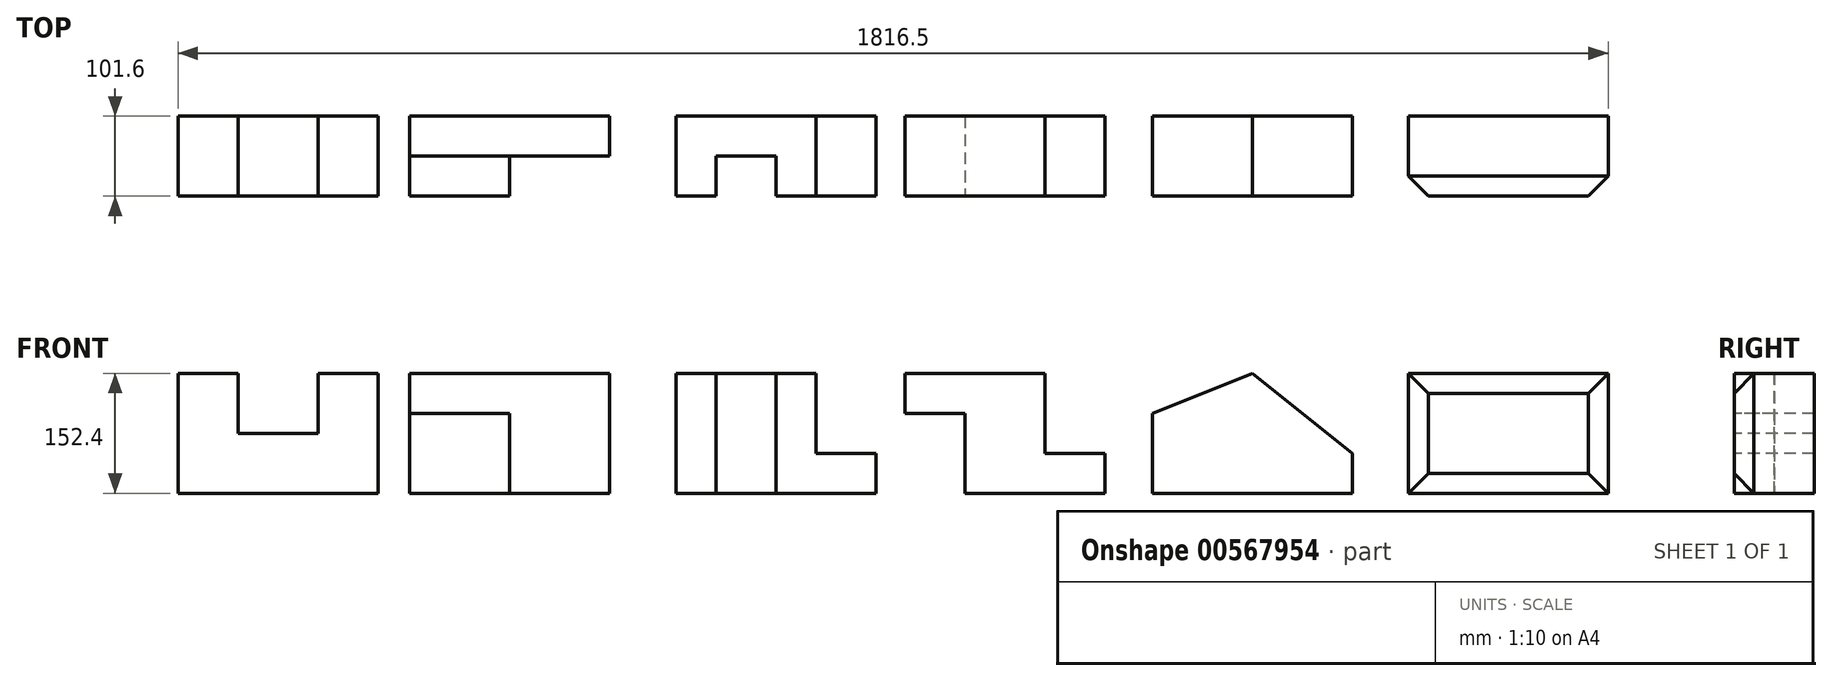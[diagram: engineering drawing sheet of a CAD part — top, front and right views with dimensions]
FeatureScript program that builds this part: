
annotation { "Feature Type Name" : "Feature", "Feature Type Description" : "" }
export const myFeature = defineFeature(function(context is Context, id is Id, definition is map)
    precondition{}
    {
        {
            var Q0;
            Q0=qCreatedBy(makeId("Front.planeOp"),FACE);
            var sketch = newSketch(context, id + "F0", { "sketchPlane" : qUnion([Q0])});
            skLineSegment(sketch, "E0", {"start": v(0, 0) * mm, "end": v(127, 0) * mm});
            skLineSegment(sketch, "E1", {"start": v(0, 0) * mm, "end": v(-127, 0) * mm});
            skLineSegment(sketch, "E2", {"start": v(-127, 0) * mm, "end": v(-127, 152.4) * mm});
            skLineSegment(sketch, "E3", {"start": v(127, 0) * mm, "end": v(127, 152.4) * mm});
            skLineSegment(sketch, "E4", {"start": v(-127, 152.4) * mm, "end": v(-50.8, 152.4) * mm});
            skLineSegment(sketch, "E5", {"start": v(-50.8, 152.4) * mm, "end": v(-50.8, 76.2) * mm});
            skLineSegment(sketch, "E6", {"start": v(-50.8, 76.2) * mm, "end": v(50.8, 76.2) * mm});
            skLineSegment(sketch, "E7", {"start": v(50.8, 76.2) * mm, "end": v(50.8, 152.4) * mm});
            skLineSegment(sketch, "E8", {"start": v(50.8, 152.4) * mm, "end": v(127, 152.4) * mm});
            skSolve(sketch);
        }
        {
            var Q0;
            Q0 = qSketchRegion(id + "F0", true);
            extrude(context, id + "F1", {"entities" : qUnion([Q0]), "oppositeDirection" : true, "depth" : 101.6 * mm, "offsetDistance" : 25.4 * mm});
        }
        {
            var Q0;
            Q0=qCreatedBy(makeId("Top.planeOp"),FACE);
            var sketch = newSketch(context, id + "F2", { "sketchPlane" : qUnion([Q0])});
            skLineSegment(sketch, "E9", {"start": v(166.82, 0) * mm, "end": v(166.82, 101.6) * mm});
            skLineSegment(sketch, "E10", {"start": v(166.82, 101.6) * mm, "end": v(420.82, 101.6) * mm});
            skLineSegment(sketch, "E11", {"start": v(420.82, 101.6) * mm, "end": v(420.82, 50.8) * mm});
            skLineSegment(sketch, "E12", {"start": v(420.82, 50.8) * mm, "end": v(293.82, 50.8) * mm});
            skLineSegment(sketch, "E13", {"start": v(293.82, 50.8) * mm, "end": v(293.82, 0) * mm});
            skLineSegment(sketch, "E14", {"start": v(293.82, 0) * mm, "end": v(166.82, 0) * mm});
            skSolve(sketch);
        }
        {
            var Q0;
            Q0=makeQuery(id+"F2.imprint","IMPRINT",FACE,{"disambiguationData":[TD([[makeQuery(id+"F2.imprint","IMPRINT",EDGE,{"derivedFrom":sQuery(id+"F2.wireOp",EDGE,"E9")}),-1.0]])]});
            extrude(context, id + "F3", {"entities" : qUnion([Q0]), "depth" : 152.4 * mm, "offsetDistance" : 25.4 * mm});
        }
        {
            var Q0;
            Q0=makeQuery(id+"F3.opExtrude","SWEPT_FACE",FACE,{"disambiguationData":[OSD([sQuery(id+"F2.wireOp",EDGE,"E14")])]});
            extrude(context, id + "F4", {"entities" : qUnion([Q0]), "operationType" : NewBodyOperationType.REMOVE, "oppositeDirection" : true, "depth" : 25.4 * mm, "offsetDistance" : 25.4 * mm});
        }
        {
            var Q0;
            Q0=makeQuery(id+"F4.boolean.opBoolean","COPY",FACE,{"derivedFrom":makeQuery(id+"F4.opExtrude","CAP_FACE",FACE,{"disambiguationData":[OSD([sQuery(id+"F2.wireOp",EDGE,"E14")])],"isStart":false})});
            var sketch = newSketch(context, id + "F5", { "sketchPlane" : qUnion([Q0])});
            skLineSegment(sketch, "E15", {"start": v(166.82, 101.6) * mm, "end": v(166.82, 152.4) * mm});
            skLineSegment(sketch, "E16", {"start": v(166.82, 101.6) * mm, "end": v(293.82, 101.6) * mm});
            skSolve(sketch);
        }
        {
            var Q0;
            Q0=makeQuery(id+"F5.imprint","IMPRINT",FACE,{"disambiguationData":[TD([[makeQuery(id+"F5.imprint","IMPRINT",EDGE,{"derivedFrom":sQuery(id+"F5.wireOp",EDGE,"E15")}),1.0]])]});
            extrude(context, id + "F6", {"entities" : qUnion([Q0]), "operationType" : NewBodyOperationType.REMOVE, "oppositeDirection" : true, "depth" : 25.4 * mm, "offsetDistance" : 25.4 * mm});
        }
        {
            var Q0;
            Q0=makeQuery(id+"F4.boolean.opBoolean","COPY",FACE,{"derivedFrom":makeQuery(id+"F4.opExtrude","CAP_FACE",FACE,{"disambiguationData":[OSD([sQuery(id+"F2.wireOp",EDGE,"E14")])],"isStart":false})});
            extrude(context, id + "F7", {"entities" : qUnion([Q0]), "operationType" : NewBodyOperationType.ADD, "depth" : 25.4 * mm, "offsetDistance" : 25.4 * mm});
        }
        {
            var Q0;
            Q0=qCreatedBy(makeId("Front.planeOp"),FACE);
            var sketch = newSketch(context, id + "F8", { "sketchPlane" : qUnion([Q0])});
            skLineSegment(sketch, "E17", {"start": v(505.74, 0) * mm, "end": v(505.74, 152.4) * mm});
            skLineSegment(sketch, "E18", {"start": v(505.74, 152.4) * mm, "end": v(683.54, 152.4) * mm});
            skLineSegment(sketch, "E19", {"start": v(505.74, 0) * mm, "end": v(759.74, 0) * mm});
            skLineSegment(sketch, "E20", {"start": v(759.74, 0) * mm, "end": v(759.74, 50.8) * mm});
            skLineSegment(sketch, "E21", {"start": v(759.74, 50.8) * mm, "end": v(683.54, 50.8) * mm});
            skLineSegment(sketch, "E22", {"start": v(683.54, 50.8) * mm, "end": v(683.54, 152.4) * mm});
            skSolve(sketch);
        }
        {
            var Q0;
            Q0=makeQuery(id+"F8.imprint","IMPRINT",FACE,{"disambiguationData":[TD([[makeQuery(id+"F8.imprint","IMPRINT",EDGE,{"derivedFrom":sQuery(id+"F8.wireOp",EDGE,"E17")}),-1.0]])]});
            extrude(context, id + "F9", {"entities" : qUnion([Q0]), "oppositeDirection" : true, "depth" : 101.6 * mm, "offsetDistance" : 25.4 * mm});
        }
        {
            var Q0;
            Q0=makeQuery(id+"F9.opExtrude","CAP_FACE",FACE,{"disambiguationData":[OSD([sQuery(id+"F8.wireOp",EDGE,"E17"),sQuery(id+"F8.wireOp",EDGE,"E18"),sQuery(id+"F8.wireOp",EDGE,"E19"),sQuery(id+"F8.wireOp",EDGE,"E20"),sQuery(id+"F8.wireOp",EDGE,"E21"),sQuery(id+"F8.wireOp",EDGE,"E22")])],"isStart":true});
            var sketch = newSketch(context, id + "F10", { "sketchPlane" : qUnion([Q0])});
            skLineSegment(sketch, "E23", {"start": v(505.74, 0) * mm, "end": v(556.54, 0) * mm});
            skLineSegment(sketch, "E24", {"start": v(556.54, 0) * mm, "end": v(556.54, 152.4) * mm});
            skLineSegment(sketch, "E25", {"start": v(556.54, 152.4) * mm, "end": v(632.74, 152.4) * mm});
            skLineSegment(sketch, "E26", {"start": v(632.74, 152.4) * mm, "end": v(632.74, 0) * mm});
            skLineSegment(sketch, "E27", {"start": v(632.74, 0) * mm, "end": v(556.54, 0) * mm});
            skSolve(sketch);
        }
        {
            var Q0;
            Q0=makeQuery(id+"F10.imprint","IMPRINT",FACE,{"disambiguationData":[TD([[makeQuery(id+"F10.imprint","IMPRINT",EDGE,{"derivedFrom":sQuery(id+"F10.wireOp",EDGE,"E24")}),-1.0]])]});
            extrude(context, id + "F11", {"entities" : qUnion([Q0]), "operationType" : NewBodyOperationType.REMOVE, "oppositeDirection" : true, "depth" : 50.8 * mm, "offsetDistance" : 25.4 * mm});
        }
        {
            var Q0;
            Q0=qCreatedBy(makeId("Front.planeOp"),FACE);
            var sketch = newSketch(context, id + "F12", { "sketchPlane" : qUnion([Q0])});
            skLineSegment(sketch, "E28", {"start": v(796.1, 152.4) * mm, "end": v(796.1, 101.6) * mm});
            skLineSegment(sketch, "E29", {"start": v(796.1, 152.4) * mm, "end": v(973.9, 152.4) * mm});
            skLineSegment(sketch, "E30", {"start": v(973.9, 152.4) * mm, "end": v(973.9, 50.8) * mm});
            skLineSegment(sketch, "E31", {"start": v(973.9, 50.8) * mm, "end": v(1050.1, 50.8) * mm});
            skLineSegment(sketch, "E32", {"start": v(1050.1, 50.8) * mm, "end": v(1050.1, 0) * mm});
            skLineSegment(sketch, "E33", {"start": v(1050.1, 0) * mm, "end": v(872.3, 0) * mm});
            skLineSegment(sketch, "E34", {"start": v(872.3, 0) * mm, "end": v(872.3, 101.6) * mm});
            skLineSegment(sketch, "E35", {"start": v(872.3, 101.6) * mm, "end": v(796.1, 101.6) * mm});
            skSolve(sketch);
        }
        {
            var Q0;
            Q0=makeQuery(id+"F12.imprint","IMPRINT",FACE,{"disambiguationData":[TD([[makeQuery(id+"F12.imprint","IMPRINT",EDGE,{"derivedFrom":sQuery(id+"F12.wireOp",EDGE,"E28")}),1.0]])]});
            extrude(context, id + "F13", {"entities" : qUnion([Q0]), "oppositeDirection" : true, "depth" : 101.6 * mm, "offsetDistance" : 25.4 * mm});
        }
        {
            var Q0;
            Q0=qCreatedBy(makeId("Front.planeOp"),FACE);
            var sketch = newSketch(context, id + "F14", { "sketchPlane" : qUnion([Q0])});
            skLineSegment(sketch, "E36", {"start": v(1110.53, 0) * mm, "end": v(1110.53, 101.6) * mm});
            skLineSegment(sketch, "E37", {"start": v(1110.53, 0) * mm, "end": v(1237.53, 0) * mm});
            skLineSegment(sketch, "E38", {"start": v(1237.53, 152.4) * mm, "end": v(1110.53, 101.6) * mm});
            skLineSegment(sketch, "E39", {"start": v(1237.53, 0) * mm, "end": v(1364.53, 0) * mm});
            skLineSegment(sketch, "E40", {"start": v(1364.53, 0) * mm, "end": v(1364.53, 50.8) * mm});
            skLineSegment(sketch, "E41", {"start": v(1364.53, 50.8) * mm, "end": v(1237.53, 152.4) * mm});
            skSolve(sketch);
        }
        {
            var Q0;
            Q0 = qSketchRegion(id + "F14", true);
            var Q1;
            Q1=makeQuery(id+"F14.imprint","IMPRINT",FACE,{"disambiguationData":[TD([[makeQuery(id+"F14.imprint","IMPRINT",EDGE,{"derivedFrom":sQuery(id+"F14.wireOp",EDGE,"E36")}),-1.0]])]});
            extrude(context, id + "F15", {"entities" : qUnion([Q0, Q1]), "oppositeDirection" : true, "depth" : 101.6 * mm, "offsetDistance" : 25.4 * mm});
        }
        {
            var Q0;
            Q0=qCreatedBy(makeId("Front.planeOp"),FACE);
            var sketch = newSketch(context, id + "F16", { "sketchPlane" : qUnion([Q0])});
            skLineSegment(sketch, "E42", {"start": v(1435.5, 0) * mm, "end": v(1435.5, 152.4) * mm});
            skLineSegment(sketch, "E43", {"start": v(1435.5, 152.4) * mm, "end": v(1689.5, 152.4) * mm});
            skLineSegment(sketch, "E44", {"start": v(1689.5, 152.4) * mm, "end": v(1689.5, 0) * mm});
            skLineSegment(sketch, "E45", {"start": v(1689.5, 0) * mm, "end": v(1435.5, 0) * mm});
            skLineSegment(sketch, "E46", {"start": v(1435.5, 0) * mm, "end": v(1460.9, 0) * mm});
            skLineSegment(sketch, "E47", {"start": v(1460.9, 127) * mm, "end": v(1664.1, 127) * mm});
            skLineSegment(sketch, "E48", {"start": v(1664.1, 127) * mm, "end": v(1664.1, 25.4) * mm});
            skLineSegment(sketch, "E49", {"start": v(1664.1, 25.4) * mm, "end": v(1460.9, 25.4) * mm});
            skLineSegment(sketch, "E50", {"start": v(1460.9, 25.4) * mm, "end": v(1460.9, 127) * mm});
            skSolve(sketch);
        }
        {
            var Q0;
            Q0=makeQuery(id+"F16.imprint","IMPRINT",FACE,{"disambiguationData":[TD([[makeQuery(id+"F16.imprint","IMPRINT",EDGE,{"derivedFrom":sQuery(id+"F16.wireOp",EDGE,"E42")}),-1.0]])]});
            var Q1;
            Q1=makeQuery(id+"F16.imprint","IMPRINT",FACE,{"disambiguationData":[TD([[makeQuery(id+"F16.imprint","IMPRINT",EDGE,{"derivedFrom":sQuery(id+"F16.wireOp",EDGE,"E47")}),-1.0]])]});
            extrude(context, id + "F17", {"entities" : qUnion([Q0, Q1]), "oppositeDirection" : true, "depth" : 101.6 * mm, "offsetDistance" : 25.4 * mm});
        }
        {
            var Q0;
            Q0=makeQuery(id+"F17.opExtrude","CAP_FACE",FACE,{"disambiguationData":[OSD([sQuery(id+"F16.wireOp",EDGE,"E42"),sQuery(id+"F16.wireOp",EDGE,"E43"),sQuery(id+"F16.wireOp",EDGE,"E44"),sQuery(id+"F16.wireOp",EDGE,"E45"),sQuery(id+"F16.wireOp",EDGE,"E46")])],"isStart":true});
            chamfer(context, id + "F18", {"entities" : qUnion([Q0]), "width" : 25.4 * mm, "tangentPropagation" : true});
        }
    });
